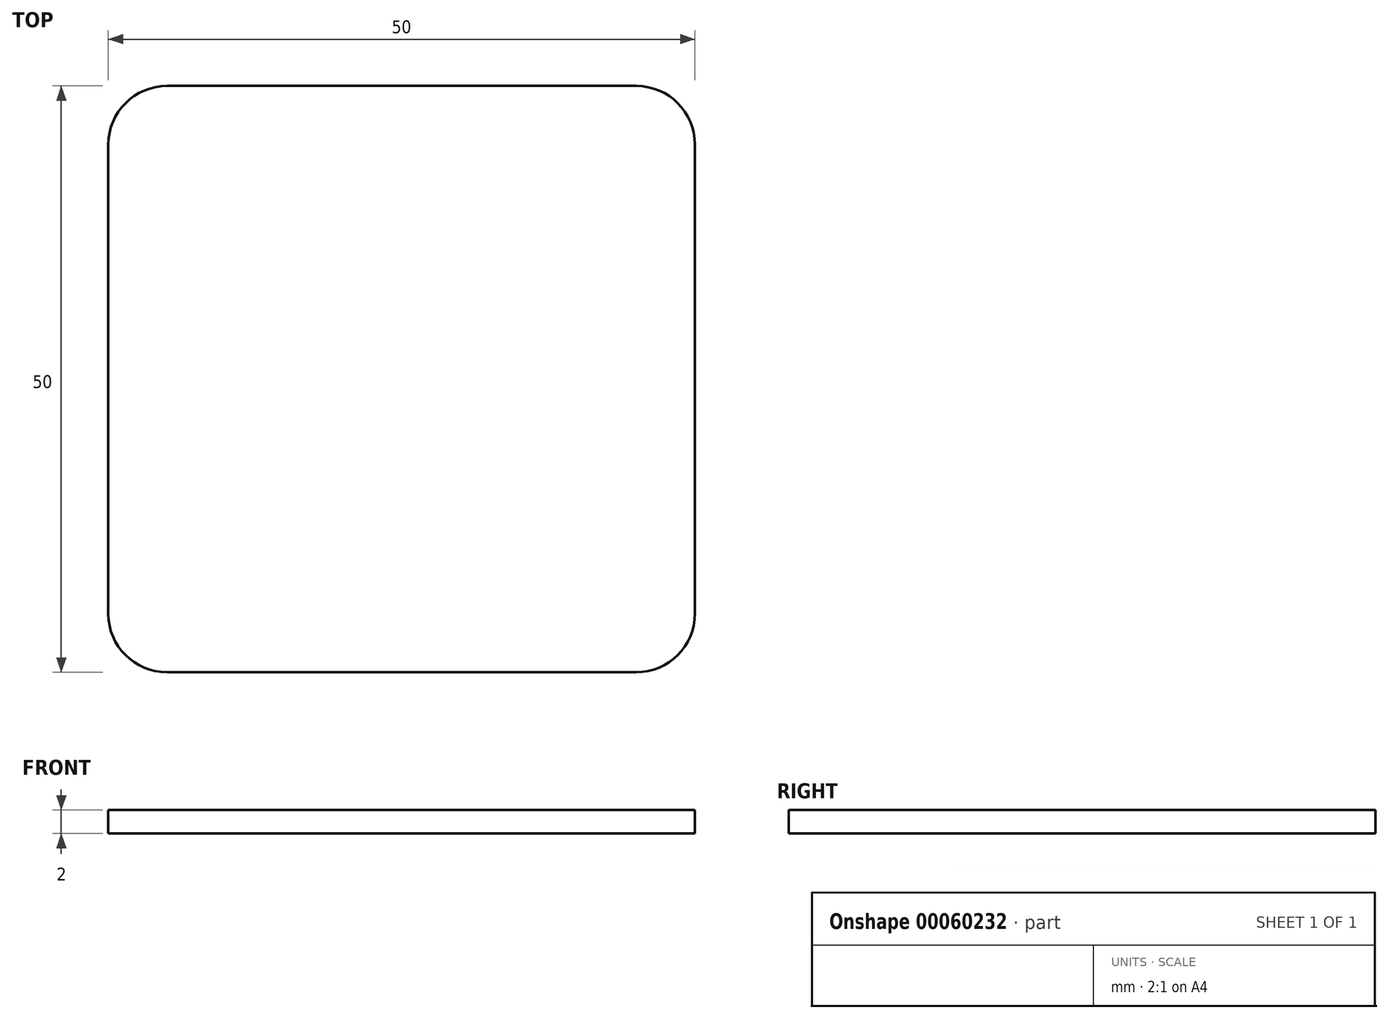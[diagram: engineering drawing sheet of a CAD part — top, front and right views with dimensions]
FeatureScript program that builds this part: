
annotation { "Feature Type Name" : "Feature", "Feature Type Description" : "" }
export const myFeature = defineFeature(function(context is Context, id is Id, definition is map)
    precondition{}
    {
        {
            var Q0;
            Q0=qCreatedBy(makeId("Top.planeOp"),FACE);
            var sketch = newSketch(context, id + "F0", { "sketchPlane" : qUnion([Q0])});
            skLineSegment(sketch, "E0.bottom", {"start": v(0, 0) * mm, "end": v(50, 0) * mm});
            skLineSegment(sketch, "E0.top", {"start": v(0, -50) * mm, "end": v(50, -50) * mm});
            skLineSegment(sketch, "E0.left", {"start": v(0, 0) * mm, "end": v(0, -50) * mm});
            skLineSegment(sketch, "E0.right", {"start": v(50, 0) * mm, "end": v(50, -50) * mm});
            skSolve(sketch);
        }
        {
            var Q0;
            Q0 = qSketchRegion(id + "F0", true);
            extrude(context, id + "F1", {"entities" : qUnion([Q0]), "depth" : 2 * mm});
        }
        {
            var Q0;
            Q0=makeQuery(id+"F1.opExtrude","SWEPT_EDGE",EDGE,{"disambiguationData":[OSD([sQuery(id+"F0.wireOp",EDGE,"E0.top"),sQuery(id+"F0.wireOp",EDGE,"E0.left")])]});
            var Q1;
            Q1=makeQuery(id+"F1.opExtrude","SWEPT_EDGE",EDGE,{"disambiguationData":[OSD([sQuery(id+"F0.wireOp",EDGE,"E0.top"),sQuery(id+"F0.wireOp",EDGE,"E0.right")])]});
            var Q2;
            Q2=makeQuery(id+"F1.opExtrude","SWEPT_EDGE",EDGE,{"disambiguationData":[OSD([sQuery(id+"F0.wireOp",EDGE,"E0.bottom"),sQuery(id+"F0.wireOp",EDGE,"E0.right")])]});
            var Q3;
            Q3=makeQuery(id+"F1.opExtrude","SWEPT_EDGE",EDGE,{"disambiguationData":[OSD([sQuery(id+"F0.wireOp",EDGE,"E0.bottom"),sQuery(id+"F0.wireOp",EDGE,"E0.left")])]});
            fillet(context, id + "F2", {"entities" : qUnion([Q0, Q1, Q2, Q3]), "radius" : 5 * mm, "tangentPropagation" : true, "allowEdgeOverflow" : false});
        }
    });
